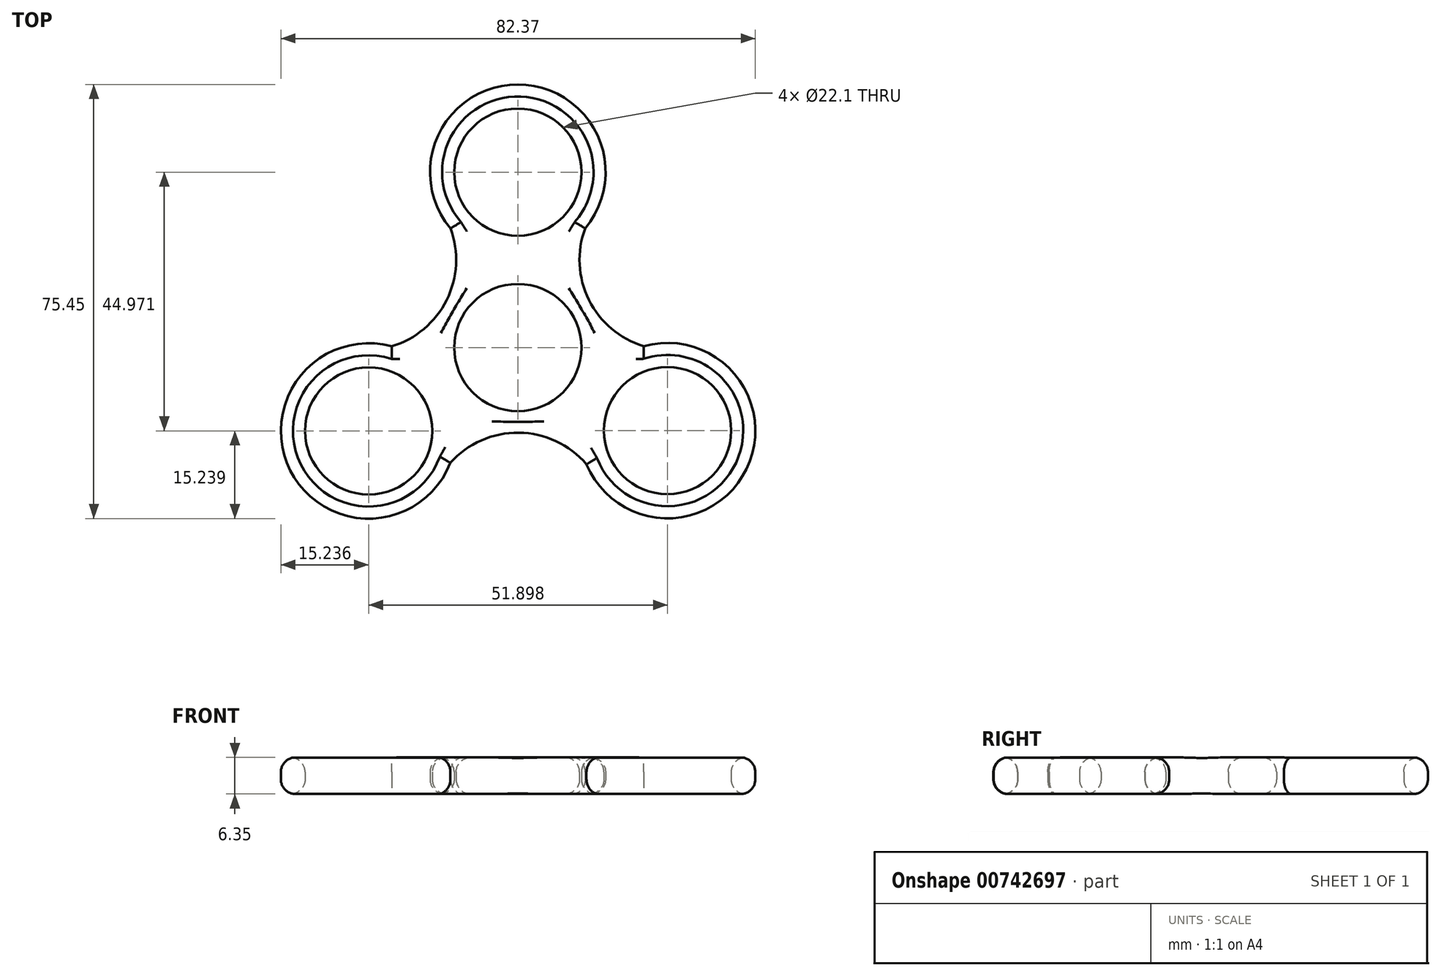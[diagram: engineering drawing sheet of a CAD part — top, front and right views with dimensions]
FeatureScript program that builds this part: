
annotation { "Feature Type Name" : "Feature", "Feature Type Description" : "" }
export const myFeature = defineFeature(function(context is Context, id is Id, definition is map)
    precondition{}
    {
        {
            var Q0;
            Q0=qCreatedBy(makeId("Top.planeOp"),FACE);
            var sketch = newSketch(context, id + "F0", { "sketchPlane" : qUnion([Q0])});
            skCircle(sketch, "E0", {"center": v(0, 0) * mm, "radius": 11.05 * mm});
            skCircle(sketch, "E1", {"center": v(0, 30.48) * mm, "radius": 11.05 * mm});
            skArc(sketch, "E2", {"start": v(11.7, 20.7) * mm, "mid": v(0, 45.72) * mm, "end": v(-11.7, 20.7) * mm});
            skCircle(sketch, "E3.1.0", {"center": v(-25.9, -14.5) * mm, "radius": 11.05 * mm});
            skArc(sketch, "E3.1.1", {"start": v(-21.9, 0.21) * mm, "mid": v(-39.52, -21.34) * mm, "end": v(-11.71, -20.05) * mm});
            skCircle(sketch, "E3.2.0", {"center": v(26, -14.44) * mm, "radius": 11.05 * mm});
            skArc(sketch, "E3.2.1", {"start": v(11.92, -20.29) * mm, "mid": v(39.71, -21.08) * mm, "end": v(21.85, 0.23) * mm});
            skPoint(sketch, "E3.center", {"position": v(0.03, 0.52) * mm});
            skArc(sketch, "E4", {"start": v(-30.4, 0.07) * mm, "mid": v(-14.77, 4.7) * mm, "end": v(-11.7, 20.7) * mm});
            skArc(sketch, "E5.2.0", {"start": v(11.7, 20.7) * mm, "mid": v(12.81, 7.4) * mm, "end": v(23.78, -0.23) * mm});
            skArc(sketch, "E6.trimOffspring", {"start": v(11.92, -20.29) * mm, "mid": v(-0.13, -14.8) * mm, "end": v(-12.09, -20.48) * mm});
            skPoint(sketch, "E7.orphan", {"position": v(15.26, 26.28) * mm});
            skSolve(sketch);
        }
        {
            var Q0;
            Q0 = qSketchRegion(id + "F0", true);
            extrude(context, id + "F1", {"entities" : qUnion([Q0]), "depth" : 6.35 * mm, "offsetDistance" : 25.4 * mm});
        }
        {
            var Q0;
            Q0=makeQuery(id+"F1.opExtrude","CAP_FACE",FACE,{"disambiguationData":[OSD([sQuery(id+"F0.wireOp",EDGE,"E0"),sQuery(id+"F0.wireOp",EDGE,"E1"),sQuery(id+"F0.wireOp",EDGE,"E2"),sQuery(id+"F0.wireOp",EDGE,"E3.1.0"),sQuery(id+"F0.wireOp",EDGE,"E3.1.1"),sQuery(id+"F0.wireOp",EDGE,"E3.2.0"),sQuery(id+"F0.wireOp",EDGE,"E3.2.1"),sQuery(id+"F0.wireOp",EDGE,"E4"),sQuery(id+"F0.wireOp",EDGE,"E5.2.0"),sQuery(id+"F0.wireOp",EDGE,"E6.trimOffspring")])],"isStart":false});
            var Q1;
            Q1=makeQuery(id+"F1.opExtrude","CAP_FACE",FACE,{"disambiguationData":[OSD([sQuery(id+"F0.wireOp",EDGE,"E0"),sQuery(id+"F0.wireOp",EDGE,"E1"),sQuery(id+"F0.wireOp",EDGE,"E2"),sQuery(id+"F0.wireOp",EDGE,"E3.1.0"),sQuery(id+"F0.wireOp",EDGE,"E3.1.1"),sQuery(id+"F0.wireOp",EDGE,"E3.2.0"),sQuery(id+"F0.wireOp",EDGE,"E3.2.1"),sQuery(id+"F0.wireOp",EDGE,"E4"),sQuery(id+"F0.wireOp",EDGE,"E5.2.0"),sQuery(id+"F0.wireOp",EDGE,"E6.trimOffspring")])],"isStart":true});
            fillet(context, id + "F2", {"entities" : qUnion([Q0, Q1]), "radius" : 2.54 * mm, "tangentPropagation" : true, "allowEdgeOverflow" : false});
        }
    });
